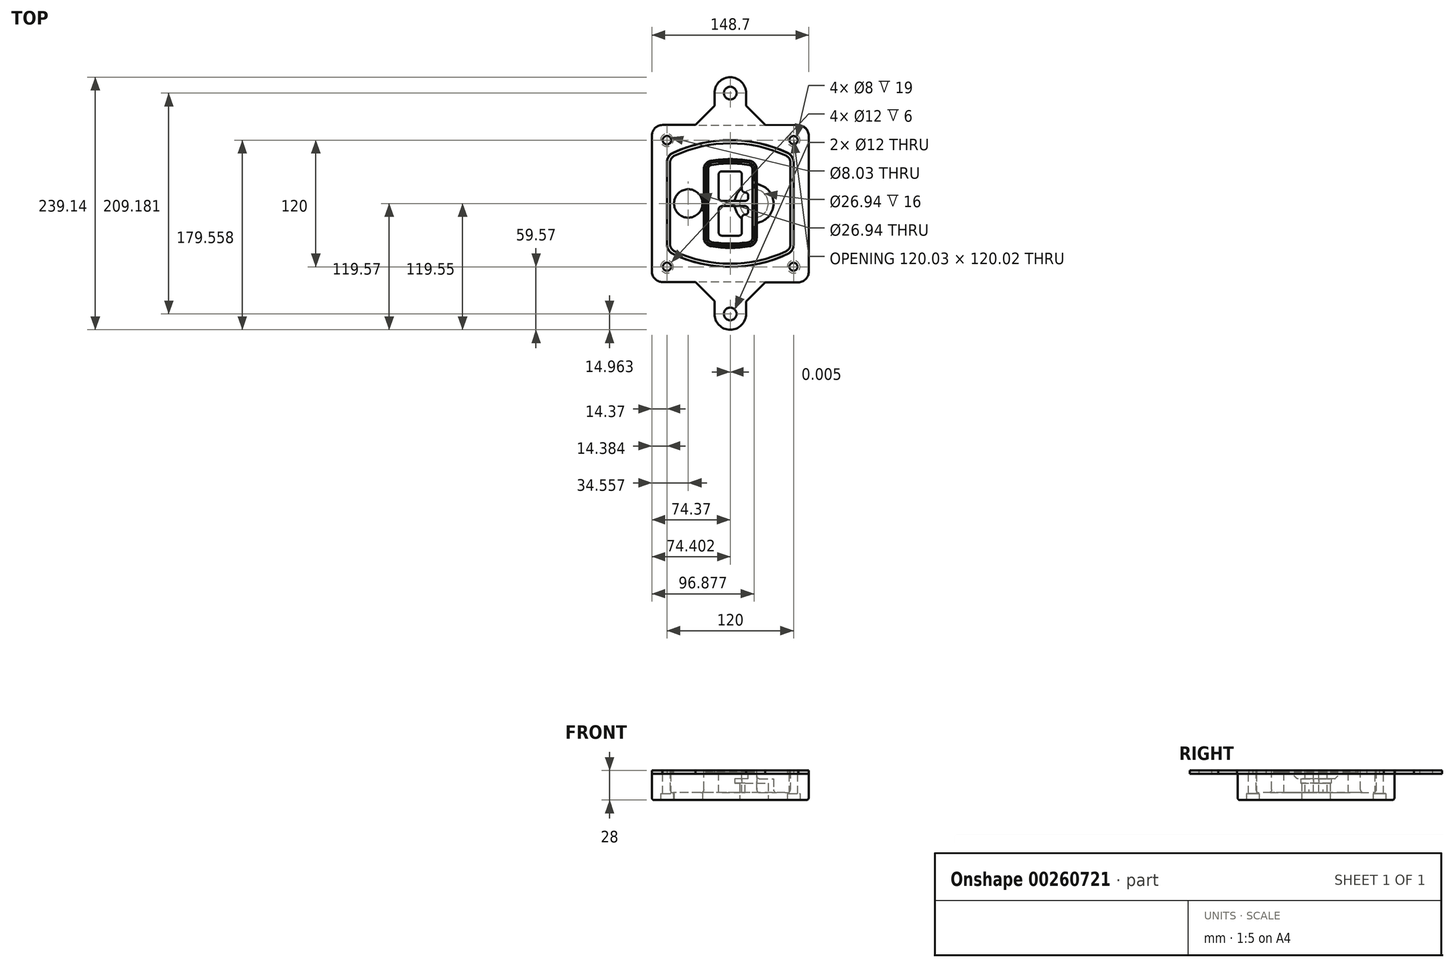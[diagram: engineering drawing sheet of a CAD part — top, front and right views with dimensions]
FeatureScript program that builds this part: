
annotation { "Feature Type Name" : "Feature", "Feature Type Description" : "" }
export const myFeature = defineFeature(function(context is Context, id is Id, definition is map)
    precondition{}
    {
        {
            var Q0;
            Q0=qCreatedBy(makeId("Top.planeOp"),FACE);
            var sketch = newSketch(context, id + "F0", { "sketchPlane" : qUnion([Q0])});
            skPoint(sketch, "E0.rect.middle", {"position": v(0, 0) * mm});
            skLineSegment(sketch, "E1.bottom", {"start": v(-64.25, -74.25) * mm, "end": v(64.25, -74.25) * mm});
            skLineSegment(sketch, "E1.top", {"start": v(-64.25, 74.25) * mm, "end": v(64.25, 74.25) * mm});
            skLineSegment(sketch, "E1.left", {"start": v(-74.25, -64.25) * mm, "end": v(-74.25, 64.25) * mm});
            skLineSegment(sketch, "E1.right", {"start": v(74.25, -64.25) * mm, "end": v(74.25, 64.25) * mm});
            skLineSegment(sketch, "E2", {"start": v(-74.25, 74.25) * mm, "end": v(74.25, -74.25) * mm, "construction": true});
            skLineSegment(sketch, "E3", {"start": v(74.25, 74.25) * mm, "end": v(-74.25, -74.25) * mm, "construction": true});
            skCircle(sketch, "E4", {"center": v(-60, 60) * mm, "radius": 4 * mm});
            skCircle(sketch, "E5", {"center": v(60, 60) * mm, "radius": 4 * mm});
            skCircle(sketch, "E6", {"center": v(60, -60) * mm, "radius": 4 * mm});
            skCircle(sketch, "E7", {"center": v(-60, -60) * mm, "radius": 4 * mm});
            skLineSegment(sketch, "E8", {"start": v(-60, 60) * mm, "end": v(60, 60) * mm, "construction": true});
            skLineSegment(sketch, "E9", {"start": v(60, 60) * mm, "end": v(60, -60) * mm, "construction": true});
            skLineSegment(sketch, "E10", {"start": v(60, -60) * mm, "end": v(-60, -60) * mm, "construction": true});
            skLineSegment(sketch, "E11", {"start": v(-60, -60) * mm, "end": v(-60, 60) * mm, "construction": true});
            skLineSegment(sketch, "E12", {"start": v(-60, 38.83) * mm, "end": v(-60, -38.83) * mm});
            skLineSegment(sketch, "E13", {"start": v(60, 38.83) * mm, "end": v(60, -38.83) * mm});
            skArc(sketch, "E14", {"start": v(54.26, 47.88) * mm, "mid": v(0, 60) * mm, "end": v(-54.26, 47.88) * mm});
            skArc(sketch, "E15", {"start": v(-54.26, -47.88) * mm, "mid": v(0, -60) * mm, "end": v(54.26, -47.88) * mm});
            skLineSegment(sketch, "E16", {"start": v(-60, 0) * mm, "end": v(60, 0) * mm, "construction": true});
            skPoint(sketch, "E17.visualSharp", {"position": v(-60, -45) * mm});
            skArc(sketch, "E17.filletArc", {"start": v(-60, -38.83) * mm, "mid": v(-58.44, -44.2) * mm, "end": v(-54.26, -47.88) * mm});
            skPoint(sketch, "E18.visualSharp", {"position": v(-60, 45) * mm});
            skArc(sketch, "E18.filletArc", {"start": v(-54.26, 47.88) * mm, "mid": v(-58.44, 44.2) * mm, "end": v(-60, 38.83) * mm});
            skPoint(sketch, "E19.visualSharp", {"position": v(60, 45) * mm});
            skArc(sketch, "E19.filletArc", {"start": v(60, 38.83) * mm, "mid": v(58.44, 44.2) * mm, "end": v(54.26, 47.88) * mm});
            skPoint(sketch, "E20.visualSharp", {"position": v(60, -45) * mm});
            skArc(sketch, "E20.filletArc", {"start": v(54.26, -47.88) * mm, "mid": v(58.44, -44.2) * mm, "end": v(60, -38.83) * mm});
            skPoint(sketch, "E21.visualSharp", {"position": v(-74.25, 74.25) * mm});
            skArc(sketch, "E21.filletArc", {"start": v(-64.25, 74.25) * mm, "mid": v(-71.32, 71.32) * mm, "end": v(-74.25, 64.25) * mm});
            skPoint(sketch, "E22.visualSharp", {"position": v(74.25, 74.25) * mm});
            skArc(sketch, "E22.filletArc", {"start": v(74.25, 64.25) * mm, "mid": v(71.32, 71.32) * mm, "end": v(64.25, 74.25) * mm});
            skPoint(sketch, "E23.visualSharp", {"position": v(74.25, -74.25) * mm});
            skArc(sketch, "E23.filletArc", {"start": v(64.25, -74.25) * mm, "mid": v(71.32, -71.32) * mm, "end": v(74.25, -64.25) * mm});
            skPoint(sketch, "E24.visualSharp", {"position": v(-74.25, -74.25) * mm});
            skArc(sketch, "E24.filletArc", {"start": v(-74.25, -64.25) * mm, "mid": v(-71.32, -71.32) * mm, "end": v(-64.25, -74.25) * mm});
            skArc(sketch, "E25.0", {"start": v(57, 38.83) * mm, "mid": v(55.9, 42.58) * mm, "end": v(52.98, 45.17) * mm});
            skLineSegment(sketch, "E25.1", {"start": v(57, 38.83) * mm, "end": v(57, -38.83) * mm});
            skArc(sketch, "E25.2", {"start": v(52.98, -45.17) * mm, "mid": v(55.9, -42.58) * mm, "end": v(57, -38.83) * mm});
            skArc(sketch, "E25.3", {"start": v(-52.98, -45.17) * mm, "mid": v(0, -57) * mm, "end": v(52.98, -45.17) * mm});
            skArc(sketch, "E25.4", {"start": v(-57, -38.83) * mm, "mid": v(-55.9, -42.58) * mm, "end": v(-52.98, -45.17) * mm});
            skArc(sketch, "E25.5", {"start": v(52.98, 45.17) * mm, "mid": v(0, 57) * mm, "end": v(-52.98, 45.17) * mm});
            skLineSegment(sketch, "E25.6", {"start": v(-57, 38.83) * mm, "end": v(-57, -38.83) * mm});
            skArc(sketch, "E25.7", {"start": v(-52.98, 45.17) * mm, "mid": v(-55.9, 42.58) * mm, "end": v(-57, 38.83) * mm});
            skArc(sketch, "E26.0", {"start": v(-55.96, 51.5) * mm, "mid": v(-61.82, 46.33) * mm, "end": v(-64, 38.83) * mm});
            skArc(sketch, "E26.1", {"start": v(55.96, 51.5) * mm, "mid": v(0, 64) * mm, "end": v(-55.96, 51.5) * mm});
            skArc(sketch, "E26.2", {"start": v(64, 38.83) * mm, "mid": v(61.82, 46.33) * mm, "end": v(55.96, 51.5) * mm});
            skLineSegment(sketch, "E26.3", {"start": v(64, 38.83) * mm, "end": v(64, -38.83) * mm});
            skArc(sketch, "E26.4", {"start": v(55.96, -51.5) * mm, "mid": v(61.82, -46.33) * mm, "end": v(64, -38.83) * mm});
            skLineSegment(sketch, "E26.5", {"start": v(-64, 38.83) * mm, "end": v(-64, -38.83) * mm});
            skArc(sketch, "E26.6", {"start": v(-55.96, -51.5) * mm, "mid": v(0, -64) * mm, "end": v(55.96, -51.5) * mm});
            skArc(sketch, "E26.7", {"start": v(-64, -38.83) * mm, "mid": v(-61.82, -46.33) * mm, "end": v(-55.96, -51.5) * mm});
            skSolve(sketch);
        }
        {
            var Q0;
            Q0=makeQuery(id+"F0.imprint","IMPRINT",FACE,{"disambiguationData":[TD([[makeQuery(id+"F0.imprint","IMPRINT",EDGE,{"derivedFrom":sQuery(id+"F0.wireOp",EDGE,"E1.bottom")}),1.0]])]});
            var Q1;
            Q1=makeQuery(id+"F0.imprint","IMPRINT",FACE,{"disambiguationData":[TD([[makeQuery(id+"F0.imprint","IMPRINT",EDGE,{"derivedFrom":sQuery(id+"F0.wireOp",EDGE,"E12")}),1.0]])]});
            var Q2;
            Q2=makeQuery(id+"F0.imprint","IMPRINT",FACE,{"disambiguationData":[TD([[makeQuery(id+"F0.imprint","IMPRINT",EDGE,{"derivedFrom":sQuery(id+"F0.wireOp",EDGE,"E25.0")}),1.0]])]});
            var Q3;
            Q3=makeQuery(id+"F0.imprint","IMPRINT",FACE,{"disambiguationData":[TD([[makeQuery(id+"F0.imprint","IMPRINT",EDGE,{"derivedFrom":sQuery(id+"F0.wireOp",EDGE,"E12")}),-1.0]])]});
            extrude(context, id + "F1", {"entities" : qUnion([Q0, Q1, Q2, Q3]), "oppositeDirection" : true, "depth" : 25 * mm});
        }
        {
            var Q0;
            Q0=makeQuery(id+"F0.imprint","IMPRINT",FACE,{"disambiguationData":[TD([[makeQuery(id+"F0.imprint","IMPRINT",EDGE,{"derivedFrom":sQuery(id+"F0.wireOp",EDGE,"E12")}),1.0]])]});
            extrude(context, id + "F2", {"entities" : qUnion([Q0]), "operationType" : NewBodyOperationType.ADD, "depth" : 3 * mm});
        }
        {
            var Q0;
            Q0=makeQuery(id+"F0.imprint","IMPRINT",FACE,{"disambiguationData":[TD([[makeQuery(id+"F0.imprint","IMPRINT",EDGE,{"derivedFrom":sQuery(id+"F0.wireOp",EDGE,"E25.0")}),1.0]])]});
            extrude(context, id + "F3", {"entities" : qUnion([Q0]), "operationType" : NewBodyOperationType.REMOVE, "oppositeDirection" : true, "depth" : 18 * mm});
        }
        {
            var Q0;
            Q0=makeQuery(id+"F2.opExtrude","CAP_FACE",FACE,{"disambiguationData":[OSD([sQuery(id+"F0.wireOp",EDGE,"E12"),sQuery(id+"F0.wireOp",EDGE,"E13"),sQuery(id+"F0.wireOp",EDGE,"E14"),sQuery(id+"F0.wireOp",EDGE,"E15"),sQuery(id+"F0.wireOp",EDGE,"E17.filletArc"),sQuery(id+"F0.wireOp",EDGE,"E18.filletArc"),sQuery(id+"F0.wireOp",EDGE,"E19.filletArc"),sQuery(id+"F0.wireOp",EDGE,"E20.filletArc"),sQuery(id+"F0.wireOp",EDGE,"E25.0"),sQuery(id+"F0.wireOp",EDGE,"E25.1"),sQuery(id+"F0.wireOp",EDGE,"E25.2"),sQuery(id+"F0.wireOp",EDGE,"E25.3"),sQuery(id+"F0.wireOp",EDGE,"E25.4"),sQuery(id+"F0.wireOp",EDGE,"E25.5"),sQuery(id+"F0.wireOp",EDGE,"E25.6"),sQuery(id+"F0.wireOp",EDGE,"E25.7")])],"isStart":false});
            var sketch = newSketch(context, id + "F4", { "sketchPlane" : qUnion([Q0])});
            skArc(sketch, "E27.0", {"start": v(-18.34, -40.45) * mm, "mid": v(0, -42) * mm, "end": v(18.34, -40.45) * mm});
            skArc(sketch, "E28.0", {"start": v(18.34, 40.45) * mm, "mid": v(0, 42) * mm, "end": v(-18.34, 40.45) * mm});
            skLineSegment(sketch, "E29", {"start": v(-25, 32.57) * mm, "end": v(-25, -32.57) * mm});
            skLineSegment(sketch, "E30", {"start": v(25, 32.57) * mm, "end": v(25, -32.57) * mm});
            skLineSegment(sketch, "E31", {"start": v(-25, 39.1) * mm, "end": v(25, 39.1) * mm, "construction": true});
            skLineSegment(sketch, "E32", {"start": v(-25, -39.1) * mm, "end": v(25, -39.1) * mm, "construction": true});
            skPoint(sketch, "E33.visualSharp", {"position": v(-25, 39.1) * mm});
            skArc(sketch, "E33.filletArc", {"start": v(-18.34, 40.45) * mm, "mid": v(-23.11, 37.73) * mm, "end": v(-25, 32.57) * mm});
            skPoint(sketch, "E34.visualSharp", {"position": v(25, 39.1) * mm});
            skArc(sketch, "E34.filletArc", {"start": v(25, 32.57) * mm, "mid": v(23.11, 37.73) * mm, "end": v(18.34, 40.45) * mm});
            skPoint(sketch, "E35.visualSharp", {"position": v(25, -39.1) * mm});
            skArc(sketch, "E35.filletArc", {"start": v(18.34, -40.45) * mm, "mid": v(23.11, -37.73) * mm, "end": v(25, -32.57) * mm});
            skPoint(sketch, "E36.visualSharp", {"position": v(-25, -39.1) * mm});
            skArc(sketch, "E36.filletArc", {"start": v(-25, -32.57) * mm, "mid": v(-23.11, -37.73) * mm, "end": v(-18.34, -40.45) * mm});
            skArc(sketch, "E37.0", {"start": v(52.98, 45.17) * mm, "mid": v(0, 57) * mm, "end": v(-52.98, 45.17) * mm});
            skArc(sketch, "E37.1", {"start": v(-52.98, 45.17) * mm, "mid": v(-55.9, 42.58) * mm, "end": v(-57, 38.83) * mm});
            skLineSegment(sketch, "E37.2", {"start": v(-57, 38.83) * mm, "end": v(-57, -38.83) * mm});
            skArc(sketch, "E37.3", {"start": v(-57, -38.83) * mm, "mid": v(-55.9, -42.58) * mm, "end": v(-52.98, -45.17) * mm});
            skArc(sketch, "E37.4", {"start": v(-52.98, -45.17) * mm, "mid": v(0, -57) * mm, "end": v(52.98, -45.17) * mm});
            skArc(sketch, "E37.5", {"start": v(52.98, -45.17) * mm, "mid": v(55.9, -42.58) * mm, "end": v(57, -38.83) * mm});
            skLineSegment(sketch, "E37.6", {"start": v(57, 38.83) * mm, "end": v(57, -38.83) * mm});
            skArc(sketch, "E37.7", {"start": v(57, 38.83) * mm, "mid": v(55.9, 42.58) * mm, "end": v(52.98, 45.17) * mm});
            skLineSegment(sketch, "E38.0", {"start": v(23, 32.57) * mm, "end": v(23, -32.57) * mm});
            skArc(sketch, "E38.1", {"start": v(18, -38.48) * mm, "mid": v(21.58, -36.44) * mm, "end": v(23, -32.57) * mm});
            skArc(sketch, "E38.2", {"start": v(-18, -38.48) * mm, "mid": v(0, -40) * mm, "end": v(18, -38.48) * mm});
            skArc(sketch, "E38.3", {"start": v(-23, -32.57) * mm, "mid": v(-21.58, -36.44) * mm, "end": v(-18, -38.48) * mm});
            skLineSegment(sketch, "E38.4", {"start": v(-23, 32.57) * mm, "end": v(-23, -32.57) * mm});
            skArc(sketch, "E38.5", {"start": v(23, 32.57) * mm, "mid": v(21.58, 36.44) * mm, "end": v(18, 38.48) * mm});
            skArc(sketch, "E38.6", {"start": v(-18, 38.48) * mm, "mid": v(-21.58, 36.44) * mm, "end": v(-23, 32.57) * mm});
            skArc(sketch, "E38.7", {"start": v(18, 38.48) * mm, "mid": v(0, 40) * mm, "end": v(-18, 38.48) * mm});
            skArc(sketch, "E39.0", {"start": v(21, 32.57) * mm, "mid": v(20.06, 35.15) * mm, "end": v(17.67, 36.5) * mm});
            skLineSegment(sketch, "E39.1", {"start": v(21, 32.57) * mm, "end": v(21, -32.57) * mm});
            skArc(sketch, "E39.2", {"start": v(17.67, -36.5) * mm, "mid": v(20.06, -35.15) * mm, "end": v(21, -32.57) * mm});
            skArc(sketch, "E39.3", {"start": v(-17.67, -36.5) * mm, "mid": v(0, -38) * mm, "end": v(17.67, -36.5) * mm});
            skArc(sketch, "E39.4", {"start": v(-21, -32.57) * mm, "mid": v(-20.06, -35.15) * mm, "end": v(-17.67, -36.5) * mm});
            skArc(sketch, "E39.5", {"start": v(17.67, 36.5) * mm, "mid": v(0, 38) * mm, "end": v(-17.67, 36.5) * mm});
            skLineSegment(sketch, "E39.6", {"start": v(-21, 32.57) * mm, "end": v(-21, -32.57) * mm});
            skArc(sketch, "E39.7", {"start": v(-17.67, 36.5) * mm, "mid": v(-20.06, 35.15) * mm, "end": v(-21, 32.57) * mm});
            skLineSegment(sketch, "E40", {"start": v(-25, 0) * mm, "end": v(25, 0) * mm, "construction": true});
            skLineSegment(sketch, "E41", {"start": v(-11, 5.5) * mm, "end": v(-11, 27.5) * mm});
            skLineSegment(sketch, "E42", {"start": v(-8, 30.5) * mm, "end": v(8, 30.5) * mm});
            skLineSegment(sketch, "E43", {"start": v(11, 27.5) * mm, "end": v(11, 13.5) * mm});
            skLineSegment(sketch, "E44", {"start": v(14, 10.5) * mm, "end": v(14, 10.5) * mm});
            skLineSegment(sketch, "E45", {"start": v(17, 7.5) * mm, "end": v(17, 5.5) * mm});
            skLineSegment(sketch, "E46", {"start": v(14, 2.5) * mm, "end": v(-8, 2.5) * mm});
            skPoint(sketch, "E47.visualSharp", {"position": v(-11, 30.5) * mm});
            skArc(sketch, "E47.filletArc", {"start": v(-8, 30.5) * mm, "mid": v(-10.12, 29.62) * mm, "end": v(-11, 27.5) * mm});
            skPoint(sketch, "E48.visualSharp", {"position": v(11, 30.5) * mm});
            skArc(sketch, "E48.filletArc", {"start": v(11, 27.5) * mm, "mid": v(10.12, 29.62) * mm, "end": v(8, 30.5) * mm});
            skPoint(sketch, "E49.visualSharp", {"position": v(11, 10.5) * mm});
            skArc(sketch, "E49.filletArc", {"start": v(11, 13.5) * mm, "mid": v(11.88, 11.38) * mm, "end": v(14, 10.5) * mm});
            skPoint(sketch, "E50.visualSharp", {"position": v(17, 10.5) * mm});
            skArc(sketch, "E50.filletArc", {"start": v(17, 7.5) * mm, "mid": v(16.12, 9.62) * mm, "end": v(14, 10.5) * mm});
            skPoint(sketch, "E51.visualSharp", {"position": v(17, 2.5) * mm});
            skArc(sketch, "E51.filletArc", {"start": v(14, 2.5) * mm, "mid": v(16.12, 3.38) * mm, "end": v(17, 5.5) * mm});
            skPoint(sketch, "E52.visualSharp", {"position": v(-11, 2.5) * mm});
            skArc(sketch, "E52.filletArc", {"start": v(-11, 5.5) * mm, "mid": v(-10.12, 3.38) * mm, "end": v(-8, 2.5) * mm});
            skLineSegment(sketch, "E53.0.MirrorCS", {"start": v(14, -2.5) * mm, "end": v(-8, -2.5) * mm});
            skArc(sketch, "E54.0.MirrorCS", {"start": v(-11, -5.5) * mm, "mid": v(-10.12, -3.38) * mm, "end": v(-8, -2.5) * mm});
            skLineSegment(sketch, "E55.0.MirrorCS", {"start": v(-11, -5.5) * mm, "end": v(-11, -27.5) * mm});
            skArc(sketch, "E56.0.MirrorCS", {"start": v(-8, -30.5) * mm, "mid": v(-10.12, -29.62) * mm, "end": v(-11, -27.5) * mm});
            skLineSegment(sketch, "E57.0.MirrorCS", {"start": v(-8, -30.5) * mm, "end": v(8, -30.5) * mm});
            skArc(sketch, "E58.0.MirrorCS", {"start": v(11, -27.5) * mm, "mid": v(10.12, -29.62) * mm, "end": v(8, -30.5) * mm});
            skLineSegment(sketch, "E59.0.MirrorCS", {"start": v(11, -27.5) * mm, "end": v(11, -13.5) * mm});
            skArc(sketch, "E60.0.MirrorCS", {"start": v(11, -13.5) * mm, "mid": v(11.88, -11.38) * mm, "end": v(14, -10.5) * mm});
            skArc(sketch, "E61.0.MirrorCS", {"start": v(17, -7.5) * mm, "mid": v(16.12, -9.62) * mm, "end": v(14, -10.5) * mm});
            skLineSegment(sketch, "E62.0.MirrorCS", {"start": v(17, -7.5) * mm, "end": v(17, -5.5) * mm});
            skArc(sketch, "E63.0.MirrorCS", {"start": v(14, -2.5) * mm, "mid": v(16.12, -3.38) * mm, "end": v(17, -5.5) * mm});
            skSolve(sketch);
        }
        {
            var Q0;
            Q0=makeQuery(id+"F4.imprint","IMPRINT",FACE,{"disambiguationData":[TD([[makeQuery(id+"F4.imprint","IMPRINT",EDGE,{"derivedFrom":sQuery(id+"F4.wireOp",EDGE,"E27.0")}),1.0]])]});
            var Q1;
            Q1=makeQuery(id+"F4.imprint","IMPRINT",FACE,{"disambiguationData":[TD([[makeQuery(id+"F4.imprint","IMPRINT",EDGE,{"derivedFrom":sQuery(id+"F4.wireOp",EDGE,"E38.0")}),-1.0]])]});
            var Q2;
            Q2=makeQuery(id+"F4.imprint","IMPRINT",FACE,{"disambiguationData":[TD([[makeQuery(id+"F4.imprint","IMPRINT",EDGE,{"derivedFrom":sQuery(id+"F4.wireOp",EDGE,"E39.0")}),1.0]])]});
            extrude(context, id + "F5", {"entities" : qUnion([Q0, Q1, Q2]), "operationType" : NewBodyOperationType.ADD, "endBound" : BoundingType.UP_TO_NEXT, "oppositeDirection" : true, "depth" : 25 * mm});
        }
        {
            var Q0;
            Q0=makeQuery(id+"F4.imprint","IMPRINT",FACE,{"disambiguationData":[TD([[makeQuery(id+"F4.imprint","IMPRINT",EDGE,{"derivedFrom":sQuery(id+"F4.wireOp",EDGE,"E38.0")}),-1.0]])]});
            extrude(context, id + "F6", {"entities" : qUnion([Q0]), "operationType" : NewBodyOperationType.REMOVE, "oppositeDirection" : true, "depth" : 2 * mm});
        }
        {
            var Q0;
            Q0=makeQuery(id+"F1.opExtrude","CAP_FACE",FACE,{"disambiguationData":[OSD([sQuery(id+"F0.wireOp",EDGE,"E1.bottom"),sQuery(id+"F0.wireOp",EDGE,"E1.top"),sQuery(id+"F0.wireOp",EDGE,"E1.left"),sQuery(id+"F0.wireOp",EDGE,"E1.right"),sQuery(id+"F0.wireOp",EDGE,"E4"),sQuery(id+"F0.wireOp",EDGE,"E5"),sQuery(id+"F0.wireOp",EDGE,"E6"),sQuery(id+"F0.wireOp",EDGE,"E7"),sQuery(id+"F0.wireOp",EDGE,"E21.filletArc"),sQuery(id+"F0.wireOp",EDGE,"E22.filletArc"),sQuery(id+"F0.wireOp",EDGE,"E23.filletArc"),sQuery(id+"F0.wireOp",EDGE,"E24.filletArc")])],"isStart":false});
            var sketch = newSketch(context, id + "F7", { "sketchPlane" : qUnion([Q0])});
            skCircle(sketch, "E64", {"center": v(22.5, 0) * mm, "radius": 13.47 * mm});
            skCircle(sketch, "E65", {"center": v(-39.81, 0) * mm, "radius": 13.47 * mm});
            skLineSegment(sketch, "E66", {"start": v(74.25, 0) * mm, "end": v(-74.25, 0) * mm});
            skCircle(sketch, "E67", {"center": v(22.5, 0) * mm, "radius": 18.47 * mm});
            skCircle(sketch, "E68", {"center": v(60, -60) * mm, "radius": 6 * mm});
            skCircle(sketch, "E69", {"center": v(-60, -60) * mm, "radius": 6 * mm});
            skCircle(sketch, "E70", {"center": v(-60, 60) * mm, "radius": 6 * mm});
            skCircle(sketch, "E71", {"center": v(60, 60) * mm, "radius": 6 * mm});
            skSolve(sketch);
        }
        {
            var Q0;
            {var subQ1=sQuery(id+"F7.wireOp",EDGE,"E66");var subQ4=sQuery(id+"F7.wireOp",EDGE,"E64");var subQ6=makeQuery(id+"F7.imprint","INTERSECT",VERTEX,{"disambiguationData":[OD(0.0)],"derivedFrom":[subQ4,subQ1]});Q0=makeQuery(id+"F7.imprint","IMPRINT",FACE,{"disambiguationData":[TD([[makeQuery(id+"F7.imprint","IMPRINT",EDGE,{"disambiguationData":[TD([[subQ6,-1.0]])],"derivedFrom":subQ4}),-1.0]])]});}
            var Q1;
            {var subQ0=sQuery(id+"F7.wireOp",EDGE,"E66");var subQ1=sQuery(id+"F7.wireOp",EDGE,"E64");var subQ3=makeQuery(id+"F7.imprint","INTERSECT",VERTEX,{"disambiguationData":[OD(0.0)],"derivedFrom":[subQ1,subQ0]});Q1=makeQuery(id+"F7.imprint","IMPRINT",FACE,{"disambiguationData":[TD([[makeQuery(id+"F7.imprint","IMPRINT",EDGE,{"disambiguationData":[TD([[subQ3,-1.0]])],"derivedFrom":subQ1}),1.0]])]});}
            var Q2;
            {var subQ0=sQuery(id+"F7.wireOp",EDGE,"E66");var subQ1=sQuery(id+"F7.wireOp",EDGE,"E64");var subQ3=makeQuery(id+"F7.imprint","INTERSECT",VERTEX,{"disambiguationData":[OD(0.0)],"derivedFrom":[subQ1,subQ0]});Q2=makeQuery(id+"F7.imprint","IMPRINT",FACE,{"disambiguationData":[TD([[makeQuery(id+"F7.imprint","IMPRINT",EDGE,{"disambiguationData":[TD([[subQ3,1.0]])],"derivedFrom":subQ1}),1.0]])]});}
            var Q3;
            {var subQ1=sQuery(id+"F7.wireOp",EDGE,"E66");var subQ4=sQuery(id+"F7.wireOp",EDGE,"E64");var subQ6=makeQuery(id+"F7.imprint","INTERSECT",VERTEX,{"disambiguationData":[OD(0.0)],"derivedFrom":[subQ4,subQ1]});Q3=makeQuery(id+"F7.imprint","IMPRINT",FACE,{"disambiguationData":[TD([[makeQuery(id+"F7.imprint","IMPRINT",EDGE,{"disambiguationData":[TD([[subQ6,1.0]])],"derivedFrom":subQ4}),-1.0]])]});}
            extrude(context, id + "F8", {"entities" : qUnion([Q0, Q1, Q2, Q3]), "operationType" : NewBodyOperationType.ADD, "oppositeDirection" : true, "depth" : 20 * mm});
        }
        {
            var Q0;
            {var subQ0=sQuery(id+"F7.wireOp",EDGE,"E66");var subQ1=sQuery(id+"F7.wireOp",EDGE,"E64");var subQ3=makeQuery(id+"F7.imprint","INTERSECT",VERTEX,{"disambiguationData":[OD(0.0)],"derivedFrom":[subQ1,subQ0]});Q0=makeQuery(id+"F7.imprint","IMPRINT",FACE,{"disambiguationData":[TD([[makeQuery(id+"F7.imprint","IMPRINT",EDGE,{"disambiguationData":[TD([[subQ3,-1.0]])],"derivedFrom":subQ1}),1.0]])]});}
            var Q1;
            {var subQ0=sQuery(id+"F7.wireOp",EDGE,"E66");var subQ1=sQuery(id+"F7.wireOp",EDGE,"E64");var subQ3=makeQuery(id+"F7.imprint","INTERSECT",VERTEX,{"disambiguationData":[OD(0.0)],"derivedFrom":[subQ1,subQ0]});Q1=makeQuery(id+"F7.imprint","IMPRINT",FACE,{"disambiguationData":[TD([[makeQuery(id+"F7.imprint","IMPRINT",EDGE,{"disambiguationData":[TD([[subQ3,1.0]])],"derivedFrom":subQ1}),1.0]])]});}
            extrude(context, id + "F9", {"entities" : qUnion([Q0, Q1]), "operationType" : NewBodyOperationType.REMOVE, "oppositeDirection" : true, "depth" : 16 * mm});
        }
        {
            var Q0;
            {var subQ0=sQuery(id+"F7.wireOp",EDGE,"E66");var subQ1=sQuery(id+"F7.wireOp",EDGE,"E65");var subQ3=makeQuery(id+"F7.imprint","INTERSECT",VERTEX,{"disambiguationData":[OD(0.0)],"derivedFrom":[subQ1,subQ0]});Q0=makeQuery(id+"F7.imprint","IMPRINT",FACE,{"disambiguationData":[TD([[makeQuery(id+"F7.imprint","IMPRINT",EDGE,{"disambiguationData":[TD([[subQ3,-1.0]])],"derivedFrom":subQ1}),1.0]])]});}
            var Q1;
            {var subQ0=sQuery(id+"F7.wireOp",EDGE,"E66");var subQ1=sQuery(id+"F7.wireOp",EDGE,"E65");var subQ3=makeQuery(id+"F7.imprint","INTERSECT",VERTEX,{"disambiguationData":[OD(0.0)],"derivedFrom":[subQ1,subQ0]});Q1=makeQuery(id+"F7.imprint","IMPRINT",FACE,{"disambiguationData":[TD([[makeQuery(id+"F7.imprint","IMPRINT",EDGE,{"disambiguationData":[TD([[subQ3,1.0]])],"derivedFrom":subQ1}),1.0]])]});}
            extrude(context, id + "F10", {"entities" : qUnion([Q0, Q1]), "operationType" : NewBodyOperationType.REMOVE, "oppositeDirection" : true, "depth" : 25 * mm});
        }
        {
            var Q0;
            Q0=makeQuery(id+"F7.imprint","IMPRINT",FACE,{"disambiguationData":[TD([[makeQuery(id+"F7.imprint","IMPRINT",EDGE,{"derivedFrom":sQuery(id+"F7.wireOp",EDGE,"E68")}),1.0]])]});
            var Q1;
            Q1=makeQuery(id+"F7.imprint","IMPRINT",FACE,{"disambiguationData":[TD([[makeQuery(id+"F7.imprint","IMPRINT",EDGE,{"derivedFrom":makeQuery(id+"F1.opExtrude","CAP_EDGE",EDGE,{"disambiguationData":[OSD([sQuery(id+"F0.wireOp",EDGE,"E5")])],"isStart":false})}),-1.0]])]});
            var Q2;
            Q2=makeQuery(id+"F7.imprint","IMPRINT",FACE,{"disambiguationData":[TD([[makeQuery(id+"F7.imprint","IMPRINT",EDGE,{"derivedFrom":sQuery(id+"F7.wireOp",EDGE,"E69")}),1.0]])]});
            var Q3;
            Q3=makeQuery(id+"F7.imprint","IMPRINT",FACE,{"disambiguationData":[TD([[makeQuery(id+"F7.imprint","IMPRINT",EDGE,{"derivedFrom":makeQuery(id+"F1.opExtrude","CAP_EDGE",EDGE,{"disambiguationData":[OSD([sQuery(id+"F0.wireOp",EDGE,"E4")])],"isStart":false})}),-1.0]])]});
            var Q4;
            Q4=makeQuery(id+"F7.imprint","IMPRINT",FACE,{"disambiguationData":[TD([[makeQuery(id+"F7.imprint","IMPRINT",EDGE,{"derivedFrom":sQuery(id+"F7.wireOp",EDGE,"E70")}),1.0]])]});
            var Q5;
            Q5=makeQuery(id+"F7.imprint","IMPRINT",FACE,{"disambiguationData":[TD([[makeQuery(id+"F7.imprint","IMPRINT",EDGE,{"derivedFrom":makeQuery(id+"F1.opExtrude","CAP_EDGE",EDGE,{"disambiguationData":[OSD([sQuery(id+"F0.wireOp",EDGE,"E7")])],"isStart":false})}),-1.0]])]});
            var Q6;
            Q6=makeQuery(id+"F7.imprint","IMPRINT",FACE,{"disambiguationData":[TD([[makeQuery(id+"F7.imprint","IMPRINT",EDGE,{"derivedFrom":sQuery(id+"F7.wireOp",EDGE,"E71")}),1.0]])]});
            var Q7;
            Q7=makeQuery(id+"F7.imprint","IMPRINT",FACE,{"disambiguationData":[TD([[makeQuery(id+"F7.imprint","IMPRINT",EDGE,{"derivedFrom":makeQuery(id+"F1.opExtrude","CAP_EDGE",EDGE,{"disambiguationData":[OSD([sQuery(id+"F0.wireOp",EDGE,"E6")])],"isStart":false})}),-1.0]])]});
            extrude(context, id + "F11", {"entities" : qUnion([Q0, Q1, Q2, Q3, Q4, Q5, Q6, Q7]), "operationType" : NewBodyOperationType.REMOVE, "oppositeDirection" : true, "depth" : 6 * mm});
        }
        {
            var Q0;
            Q0=makeQuery(id+"F9.boolean.opBoolean","COPY",FACE,{"derivedFrom":makeQuery(id+"F9.opExtrude","CAP_FACE",FACE,{"disambiguationData":[OSD([sQuery(id+"F7.wireOp",EDGE,"E64")])],"isStart":false})});
            var sketch = newSketch(context, id + "F12", { "sketchPlane" : qUnion([Q0])});
            skArc(sketch, "E72.0", {"start": v(11, 14.45) * mm, "mid": v(6.45, 9.13) * mm, "end": v(4.2, 2.5) * mm});
            skArc(sketch, "E72.1", {"start": v(4.2, -2.5) * mm, "mid": v(6.45, -9.13) * mm, "end": v(11, -14.45) * mm});
            skLineSegment(sketch, "E73", {"start": v(4.2, -2.5) * mm, "end": v(14, -2.5) * mm});
            skLineSegment(sketch, "E74.0", {"start": v(14, 2.5) * mm, "end": v(4.2, 2.5) * mm});
            skArc(sketch, "E74.1", {"start": v(14, 2.5) * mm, "mid": v(16.12, 3.38) * mm, "end": v(17, 5.5) * mm});
            skLineSegment(sketch, "E74.2", {"start": v(17, 7.5) * mm, "end": v(17, 5.5) * mm});
            skArc(sketch, "E74.3", {"start": v(17, 7.5) * mm, "mid": v(16.12, 9.62) * mm, "end": v(14, 10.5) * mm});
            skArc(sketch, "E74.4", {"start": v(11, 13.5) * mm, "mid": v(11.88, 11.38) * mm, "end": v(14, 10.5) * mm});
            skLineSegment(sketch, "E74.5", {"start": v(11, 14.45) * mm, "end": v(11, 13.5) * mm});
            skLineSegment(sketch, "E74.7", {"start": v(14, -2.5) * mm, "end": v(4.2, -2.5) * mm});
            skArc(sketch, "E74.8", {"start": v(14, -2.5) * mm, "mid": v(16.12, -3.38) * mm, "end": v(17, -5.5) * mm});
            skLineSegment(sketch, "E74.9", {"start": v(17, -7.5) * mm, "end": v(17, -5.5) * mm});
            skArc(sketch, "E74.10", {"start": v(17, -7.5) * mm, "mid": v(16.12, -9.62) * mm, "end": v(14, -10.5) * mm});
            skArc(sketch, "E74.11", {"start": v(11, -13.5) * mm, "mid": v(11.88, -11.38) * mm, "end": v(14, -10.5) * mm});
            skLineSegment(sketch, "E74.12", {"start": v(11, -14.45) * mm, "end": v(11, -13.5) * mm});
            skPoint(sketch, "E75.orphan", {"position": v(11, -27.5) * mm});
            skPoint(sketch, "E76.orphan", {"position": v(-8, -2.5) * mm});
            skPoint(sketch, "E77.orphan", {"position": v(-8, 2.5) * mm});
            skPoint(sketch, "E78.orphan", {"position": v(11, 27.5) * mm});
            skSolve(sketch);
        }
        {
            var Q0;
            {var subQ7=sQuery(id+"F12.wireOp",EDGE,"E72.0");var subQ14=sQuery(id+"F12.wireOp",EDGE,"E72.1");var subQ16=sQuery(id+"F12.wireOp",EDGE,"E74.1");var subQ18=sQuery(id+"F12.wireOp",EDGE,"E74.8");Q0=qUnion([makeQuery(id+"F12.imprint","IMPRINT",FACE,{"disambiguationData":[TD([[makeQuery(id+"F12.imprint","IMPRINT",EDGE,{"derivedFrom":subQ7}),1.0]])]}),makeQuery(id+"F12.imprint","IMPRINT",FACE,{"disambiguationData":[TD([[makeQuery(id+"F12.imprint","IMPRINT",EDGE,{"derivedFrom":subQ14}),1.0]])]}),makeQuery(id+"F12.imprint","IMPRINT",FACE,{"disambiguationData":[TD([[makeQuery(id+"F12.imprint","IMPRINT",EDGE,{"derivedFrom":subQ16}),1.0]])]}),makeQuery(id+"F12.imprint","IMPRINT",FACE,{"disambiguationData":[TD([[makeQuery(id+"F12.imprint","IMPRINT",EDGE,{"derivedFrom":subQ18}),-1.0]])]})]);}
            var Q1;
            Q1=makeQuery(id+"F5.boolean.opBoolean","SPLIT",FACE,{"disambiguationData":[TD([makeQuery(id+"F5.opExtrude","SWEPT_FACE",FACE,{"disambiguationData":[OSD([sQuery(id+"F4.wireOp",EDGE,"E41")])]})])],"derivedFrom":makeQuery(id+"F3.boolean.opBoolean","COPY",FACE,{"derivedFrom":makeQuery(id+"F3.opExtrude","CAP_FACE",FACE,{"disambiguationData":[OSD([sQuery(id+"F0.wireOp",EDGE,"E25.0"),sQuery(id+"F0.wireOp",EDGE,"E25.1"),sQuery(id+"F0.wireOp",EDGE,"E25.2"),sQuery(id+"F0.wireOp",EDGE,"E25.3"),sQuery(id+"F0.wireOp",EDGE,"E25.4"),sQuery(id+"F0.wireOp",EDGE,"E25.5"),sQuery(id+"F0.wireOp",EDGE,"E25.6"),sQuery(id+"F0.wireOp",EDGE,"E25.7")])],"isStart":false})})});
            extrude(context, id + "F13", {"entities" : qUnion([Q0]), "operationType" : NewBodyOperationType.REMOVE, "endBound" : BoundingType.UP_TO_SURFACE, "endBoundEntityFace" : qUnion([Q1]), "depth" : 25 * mm});
        }
        {
            var Q0;
            Q0=makeQuery(id+"F3.boolean.opBoolean","COPY",EDGE,{"derivedFrom":makeQuery(id+"F3.opExtrude","CAP_EDGE",EDGE,{"disambiguationData":[OSD([sQuery(id+"F0.wireOp",EDGE,"E25.6")])],"isStart":false})});
            var Q1;
            Q1=makeQuery(id+"F8.boolean.opBoolean","INTERSECT",EDGE,{"derivedFrom":[makeQuery(id+"F5.opExtrude","SWEPT_FACE",FACE,{"disambiguationData":[OSD([sQuery(id+"F4.wireOp",EDGE,"E30")])]}),makeQuery(id+"F8.opExtrude","CAP_FACE",FACE,{"disambiguationData":[OSD([sQuery(id+"F7.wireOp",EDGE,"E67")])],"isStart":false})]});
            var Q2;
            Q2=makeQuery(id+"F8.boolean.opBoolean","INTERSECT",EDGE,{"disambiguationData":[OD(1.0)],"derivedFrom":[makeQuery(id+"F5.opExtrude","SWEPT_FACE",FACE,{"disambiguationData":[OSD([sQuery(id+"F4.wireOp",EDGE,"E30")])]}),makeQuery(id+"F8.opExtrude","SWEPT_FACE",FACE,{"disambiguationData":[OSD([sQuery(id+"F7.wireOp",EDGE,"E67")])]})]});
            var Q3;
            {var subQ0=sQuery(id+"F4.wireOp",EDGE,"E30");Q3=makeQuery(id+"F8.boolean.opBoolean","SPLIT",EDGE,{"disambiguationData":[TD([makeQuery(id+"F5.opExtrude","SWEPT_FACE",FACE,{"disambiguationData":[OSD([sQuery(id+"F4.wireOp",EDGE,"E35.filletArc")])]})])],"derivedFrom":makeQuery(id+"F5.opExtrude","CAP_EDGE",EDGE,{"disambiguationData":[OSD([subQ0])],"isStart":false})});}
            var Q4;
            {var subQ0=sQuery(id+"F0.wireOp",EDGE,"E25.7");var subQ1=sQuery(id+"F0.wireOp",EDGE,"E25.1");var subQ2=sQuery(id+"F0.wireOp",EDGE,"E25.6");var subQ3=sQuery(id+"F0.wireOp",EDGE,"E25.5");var subQ4=sQuery(id+"F0.wireOp",EDGE,"E25.4");var subQ5=sQuery(id+"F0.wireOp",EDGE,"E25.0");var subQ6=sQuery(id+"F0.wireOp",EDGE,"E25.2");var subQ7=sQuery(id+"F0.wireOp",EDGE,"E25.3");Q4=makeQuery(id+"F8.boolean.opBoolean","INTERSECT",EDGE,{"derivedFrom":[makeQuery(id+"F5.boolean.opBoolean","SPLIT",FACE,{"disambiguationData":[TD([makeQuery(id+"F2.opExtrude","SWEPT_FACE",FACE,{"disambiguationData":[OSD([subQ5])]})])],"derivedFrom":makeQuery(id+"F3.boolean.opBoolean","COPY",FACE,{"derivedFrom":makeQuery(id+"F3.opExtrude","CAP_FACE",FACE,{"disambiguationData":[OSD([subQ5,subQ1,subQ6,subQ7,subQ4,subQ3,subQ2,subQ0])],"isStart":false})})}),makeQuery(id+"F8.opExtrude","SWEPT_FACE",FACE,{"disambiguationData":[OSD([sQuery(id+"F7.wireOp",EDGE,"E67")])]})]});}
            var Q5;
            Q5=makeQuery(id+"F8.boolean.opBoolean","INTERSECT",EDGE,{"disambiguationData":[OD(0.0)],"derivedFrom":[makeQuery(id+"F5.opExtrude","SWEPT_FACE",FACE,{"disambiguationData":[OSD([sQuery(id+"F4.wireOp",EDGE,"E30")])]}),makeQuery(id+"F8.opExtrude","SWEPT_FACE",FACE,{"disambiguationData":[OSD([sQuery(id+"F7.wireOp",EDGE,"E67")])]})]});
            fillet(context, id + "F14", {"entities" : qUnion([Q0, Q1, Q2, Q3, Q4, Q5]), "radius" : 3 * mm, "tangentPropagation" : true, "allowEdgeOverflow" : false});
        }
        {
            var Q0;
            Q0=makeQuery(id+"F1.opExtrude","CAP_EDGE",EDGE,{"disambiguationData":[OSD([sQuery(id+"F0.wireOp",EDGE,"E1.bottom")])],"isStart":false});
            fillet(context, id + "F15", {"entities" : qUnion([Q0]), "radius" : 2 * mm, "tangentPropagation" : true, "allowEdgeOverflow" : false});
        }
        {
            var Q0;
            {var subQ0=sQuery(id+"F0.wireOp",EDGE,"E22.filletArc");var subQ1=sQuery(id+"F0.wireOp",EDGE,"E7");var subQ2=sQuery(id+"F0.wireOp",EDGE,"E6");var subQ3=sQuery(id+"F0.wireOp",EDGE,"E5");var subQ4=sQuery(id+"F0.wireOp",EDGE,"E4");var subQ5=sQuery(id+"F0.wireOp",EDGE,"E1.bottom");var subQ6=sQuery(id+"F0.wireOp",EDGE,"E21.filletArc");var subQ7=sQuery(id+"F0.wireOp",EDGE,"E1.top");var subQ8=sQuery(id+"F0.wireOp",EDGE,"E1.left");var subQ9=sQuery(id+"F0.wireOp",EDGE,"E1.right");var subQ10=sQuery(id+"F0.wireOp",EDGE,"E23.filletArc");var subQ11=sQuery(id+"F0.wireOp",EDGE,"E24.filletArc");Q0=makeQuery(id+"F2.boolean.opBoolean","SPLIT",FACE,{"disambiguationData":[TD([makeQuery(id+"F1.opExtrude","SWEPT_FACE",FACE,{"disambiguationData":[OSD([subQ5])]})])],"derivedFrom":makeQuery(id+"F1.opExtrude","CAP_FACE",FACE,{"disambiguationData":[OSD([subQ5,subQ7,subQ8,subQ9,subQ4,subQ3,subQ2,subQ1,subQ6,subQ0,subQ10,subQ11])],"isStart":true})});}
            var sketch = newSketch(context, id + "F16", { "sketchPlane" : qUnion([Q0])});
            skSolve(sketch);
        }
        {
            var Q0;
            Q0=makeQuery(id+"F16.imprint","IMPRINT",FACE,{"disambiguationData":[TD([[makeQuery(id+"F16.imprint","IMPRINT",EDGE,{"derivedFrom":makeQuery(id+"F1.opExtrude","CAP_EDGE",EDGE,{"disambiguationData":[OSD([sQuery(id+"F0.wireOp",EDGE,"E1.bottom")])],"isStart":true})}),1.0]])]});
            var sketch = newSketch(context, id + "F17", { "sketchPlane" : qUnion([Q0])});
            skArc(sketch, "E79", {"start": v(-64.17, 74.37) * mm, "mid": v(-71.23, 71.47) * mm, "end": v(-74.24, 64.44) * mm});
            skArc(sketch, "E80", {"start": v(74.33, 64.29) * mm, "mid": v(71.38, 71.12) * mm, "end": v(64.62, 74.23) * mm});
            skLineSegment(sketch, "E81", {"start": v(74.33, 64.29) * mm, "end": v(74.33, -64.52) * mm});
            skArc(sketch, "E82", {"start": v(64.6, -74.75) * mm, "mid": v(71.5, -71.58) * mm, "end": v(74.33, -64.52) * mm});
            skLineSegment(sketch, "E83", {"start": v(-74.37, -64.15) * mm, "end": v(-74.24, 64.44) * mm});
            skLineSegment(sketch, "E84", {"start": v(-32.98, -74.53) * mm, "end": v(-15.02, -92.57) * mm});
            skLineSegment(sketch, "E85", {"start": v(33.01, -74.68) * mm, "end": v(14.97, -92.64) * mm});
            skLineSegment(sketch, "E86", {"start": v(0, -74.6) * mm, "end": v(-0.07, -104.6) * mm});
            skCircle(sketch, "E87", {"center": v(-0.07, -104.6) * mm, "radius": 15 * mm, "construction": true});
            skLineSegment(sketch, "E88", {"start": v(-15.07, -104.6) * mm, "end": v(-15.07, -92.57) * mm});
            skLineSegment(sketch, "E89", {"start": v(14.93, -104.6) * mm, "end": v(14.93, -92.64) * mm});
            skCircle(sketch, "E90", {"center": v(-60, -59.92) * mm, "radius": 3.88 * mm});
            skCircle(sketch, "E91", {"center": v(59.86, -59.96) * mm, "radius": 3.84 * mm});
            skCircle(sketch, "E92", {"center": v(59.97, 60) * mm, "radius": 3.92 * mm});
            skCircle(sketch, "E93", {"center": v(-59.99, 59.99) * mm, "radius": 4.01 * mm});
            skLineSegment(sketch, "E94", {"start": v(0, 0) * mm, "end": v(74.33, -0.08) * mm});
            skLineSegment(sketch, "E95.MirrorCS", {"start": v(0.15, 74.6) * mm, "end": v(0.15, 104.6) * mm});
            skLineSegment(sketch, "E96.MirrorCS", {"start": v(-32.82, 74.6) * mm, "end": v(-14.82, 92.6) * mm});
            skLineSegment(sketch, "E97.MirrorCS", {"start": v(33.17, 74.61) * mm, "end": v(15.16, 92.6) * mm});
            skLineSegment(sketch, "E98.MirrorCS", {"start": v(15.15, 104.58) * mm, "end": v(15.13, 92.6) * mm});
            skCircle(sketch, "E99.MirrorC", {"center": v(0.15, 104.6) * mm, "radius": 15 * mm, "construction": true});
            skLineSegment(sketch, "E100.MirrorCS", {"start": v(-14.85, 104.64) * mm, "end": v(-14.87, 92.6) * mm});
            skArc(sketch, "E101", {"start": v(-53.93, 48.07) * mm, "mid": v(-58.36, 44.7) * mm, "end": v(-59.93, 39.37) * mm});
            skArc(sketch, "E102", {"start": v(54.08, 48.07) * mm, "mid": v(0.07, 60) * mm, "end": v(-53.93, 48.07) * mm});
            skArc(sketch, "E103", {"start": v(60.02, 39.06) * mm, "mid": v(58.28, 44.38) * mm, "end": v(54.08, 48.07) * mm});
            skArc(sketch, "E104", {"start": v(-59.98, -39.31) * mm, "mid": v(-58.48, -44.08) * mm, "end": v(-54.9, -47.55) * mm});
            skArc(sketch, "E105", {"start": v(55.58, -47.23) * mm, "mid": v(58.75, -43.62) * mm, "end": v(60.05, -39) * mm});
            skArc(sketch, "E106", {"start": v(-54.9, -47.55) * mm, "mid": v(0.38, -60.03) * mm, "end": v(55.58, -47.23) * mm});
            skLineSegment(sketch, "E107", {"start": v(-59.93, 39.37) * mm, "end": v(-59.98, -39.31) * mm});
            skLineSegment(sketch, "E108", {"start": v(60.02, 39.06) * mm, "end": v(60.05, -39) * mm});
            skArc(sketch, "E109", {"start": v(-74.37, -64.15) * mm, "mid": v(-71.43, -71.37) * mm, "end": v(-64.28, -74.46) * mm});
            skLineSegment(sketch, "E110", {"start": v(-64.17, 74.37) * mm, "end": v(-32.82, 74.6) * mm});
            skLineSegment(sketch, "E111", {"start": v(33.17, 74.61) * mm, "end": v(64.62, 74.23) * mm});
            skLineSegment(sketch, "E112", {"start": v(-64.28, -74.46) * mm, "end": v(-32.98, -74.53) * mm});
            skLineSegment(sketch, "E113", {"start": v(33.01, -74.68) * mm, "end": v(64.6, -74.75) * mm});
            skArc(sketch, "E114", {"start": v(15.15, 104.58) * mm, "mid": v(0.18, 119.6) * mm, "end": v(-14.85, 104.64) * mm});
            skArc(sketch, "E115", {"start": v(-15.07, -104.6) * mm, "mid": v(-0.07, -119.6) * mm, "end": v(14.93, -104.6) * mm});
            skLineSegment(sketch, "E116", {"start": v(-32.82, 74.6) * mm, "end": v(33.17, 74.61) * mm});
            skLineSegment(sketch, "E117", {"start": v(-32.98, -74.53) * mm, "end": v(33.01, -74.68) * mm});
            skSolve(sketch);
        }
        {
            var Q0;
            Q0 = qSketchRegion(id + "F17", true);
            var Q1;
            Q1=makeQuery(id+"F2.opExtrude","CAP_FACE",FACE,{"disambiguationData":[OSD([sQuery(id+"F0.wireOp",EDGE,"E12"),sQuery(id+"F0.wireOp",EDGE,"E13"),sQuery(id+"F0.wireOp",EDGE,"E14"),sQuery(id+"F0.wireOp",EDGE,"E15"),sQuery(id+"F0.wireOp",EDGE,"E17.filletArc"),sQuery(id+"F0.wireOp",EDGE,"E18.filletArc"),sQuery(id+"F0.wireOp",EDGE,"E19.filletArc"),sQuery(id+"F0.wireOp",EDGE,"E20.filletArc"),sQuery(id+"F0.wireOp",EDGE,"E25.0"),sQuery(id+"F0.wireOp",EDGE,"E25.1"),sQuery(id+"F0.wireOp",EDGE,"E25.2"),sQuery(id+"F0.wireOp",EDGE,"E25.3"),sQuery(id+"F0.wireOp",EDGE,"E25.4"),sQuery(id+"F0.wireOp",EDGE,"E25.5"),sQuery(id+"F0.wireOp",EDGE,"E25.6"),sQuery(id+"F0.wireOp",EDGE,"E25.7")])],"isStart":false});
            extrude(context, id + "F18", {"entities" : qUnion([Q0]), "endBound" : BoundingType.UP_TO_SURFACE, "endBoundEntityFace" : qUnion([Q1]), "depth" : 25 * mm});
        }
        {
            var Q0;
            Q0=makeQuery(id+"F18.opExtrude","CAP_FACE",FACE,{"disambiguationData":[OSD([sQuery(id+"F17.wireOp",EDGE,"E79"),sQuery(id+"F17.wireOp",EDGE,"E80"),sQuery(id+"F17.wireOp",EDGE,"E81"),sQuery(id+"F17.wireOp",EDGE,"E82"),sQuery(id+"F17.wireOp",EDGE,"E83"),sQuery(id+"F17.wireOp",EDGE,"E90"),sQuery(id+"F17.wireOp",EDGE,"E91"),sQuery(id+"F17.wireOp",EDGE,"E92"),sQuery(id+"F17.wireOp",EDGE,"E93"),sQuery(id+"F17.wireOp",EDGE,"E101"),sQuery(id+"F17.wireOp",EDGE,"E102"),sQuery(id+"F17.wireOp",EDGE,"E103"),sQuery(id+"F17.wireOp",EDGE,"E104"),sQuery(id+"F17.wireOp",EDGE,"E105"),sQuery(id+"F17.wireOp",EDGE,"E106"),sQuery(id+"F17.wireOp",EDGE,"E107"),sQuery(id+"F17.wireOp",EDGE,"E108"),sQuery(id+"F17.wireOp",EDGE,"E109"),sQuery(id+"F17.wireOp",EDGE,"E110"),sQuery(id+"F17.wireOp",EDGE,"E111"),sQuery(id+"F17.wireOp",EDGE,"E112"),sQuery(id+"F17.wireOp",EDGE,"E113"),sQuery(id+"F17.wireOp",EDGE,"E116"),sQuery(id+"F17.wireOp",EDGE,"E117")])],"isStart":false});
            var sketch = newSketch(context, id + "F19", { "sketchPlane" : qUnion([Q0])});
            skCircle(sketch, "E118", {"center": v(0, -104.6) * mm, "radius": 6 * mm});
            skLineSegment(sketch, "E119", {"start": v(0, -74.6) * mm, "end": v(0, -104.6) * mm});
            skLineSegment(sketch, "E120", {"start": v(-32.89, -74.53) * mm, "end": v(-14.97, -92.53) * mm});
            skLineSegment(sketch, "E121", {"start": v(33.11, -74.68) * mm, "end": v(15.03, -92.68) * mm});
            skLineSegment(sketch, "E122", {"start": v(-14.97, -92.53) * mm, "end": v(-15, -104.6) * mm});
            skLineSegment(sketch, "E123", {"start": v(15.03, -92.68) * mm, "end": v(15, -104.6) * mm});
            skArc(sketch, "E124", {"start": v(-15, -104.6) * mm, "mid": v(0, -119.57) * mm, "end": v(15, -104.6) * mm});
            skLineSegment(sketch, "E125", {"start": v(0, -104.6) * mm, "end": v(0, 0) * mm});
            skLineSegment(sketch, "E126", {"start": v(0, 0) * mm, "end": v(74.33, 0) * mm});
            skLineSegment(sketch, "E127.MirrorCS", {"start": v(-14.97, 92.53) * mm, "end": v(-15, 104.6) * mm});
            skLineSegment(sketch, "E128.MirrorCS", {"start": v(-32.89, 74.53) * mm, "end": v(-14.97, 92.53) * mm});
            skLineSegment(sketch, "E129", {"start": v(-32.82, 74.6) * mm, "end": v(33.17, 74.61) * mm});
            skLineSegment(sketch, "E130", {"start": v(-32.89, -74.53) * mm, "end": v(33.11, -74.68) * mm});
            skLineSegment(sketch, "E131", {"start": v(-32.82, 74.6) * mm, "end": v(-14.97, 92.53) * mm});
            skLineSegment(sketch, "E132", {"start": v(33.17, 74.61) * mm, "end": v(-32.82, 74.6) * mm});
            skArc(sketch, "E133", {"start": v(15, 104.6) * mm, "mid": v(0, 119.57) * mm, "end": v(-15, 104.6) * mm});
            skLineSegment(sketch, "E134", {"start": v(15, 104.6) * mm, "end": v(15.03, 92.68) * mm});
            skLineSegment(sketch, "E135", {"start": v(15.03, 92.68) * mm, "end": v(33.17, 74.61) * mm});
            skCircle(sketch, "E136", {"center": v(0, 104.57) * mm, "radius": 6 * mm});
            skSolve(sketch);
        }
        {
            var Q0;
            Q0=makeQuery(id+"F19.imprint","IMPRINT",FACE,{"disambiguationData":[TD([[makeQuery(id+"F19.imprint","IMPRINT",EDGE,{"derivedFrom":sQuery(id+"F19.wireOp",EDGE,"E118")}),-1.0]])]});
            var Q1;
            Q1=makeQuery(id+"F18.opExtrude","CAP_FACE",FACE,{"disambiguationData":[OSD([sQuery(id+"F17.wireOp",EDGE,"E79"),sQuery(id+"F17.wireOp",EDGE,"E80"),sQuery(id+"F17.wireOp",EDGE,"E81"),sQuery(id+"F17.wireOp",EDGE,"E82"),sQuery(id+"F17.wireOp",EDGE,"E83"),sQuery(id+"F17.wireOp",EDGE,"E90"),sQuery(id+"F17.wireOp",EDGE,"E91"),sQuery(id+"F17.wireOp",EDGE,"E92"),sQuery(id+"F17.wireOp",EDGE,"E93"),sQuery(id+"F17.wireOp",EDGE,"E101"),sQuery(id+"F17.wireOp",EDGE,"E102"),sQuery(id+"F17.wireOp",EDGE,"E103"),sQuery(id+"F17.wireOp",EDGE,"E104"),sQuery(id+"F17.wireOp",EDGE,"E105"),sQuery(id+"F17.wireOp",EDGE,"E106"),sQuery(id+"F17.wireOp",EDGE,"E107"),sQuery(id+"F17.wireOp",EDGE,"E108"),sQuery(id+"F17.wireOp",EDGE,"E109"),sQuery(id+"F17.wireOp",EDGE,"E110"),sQuery(id+"F17.wireOp",EDGE,"E111"),sQuery(id+"F17.wireOp",EDGE,"E112"),sQuery(id+"F17.wireOp",EDGE,"E113"),sQuery(id+"F17.wireOp",EDGE,"E116"),sQuery(id+"F17.wireOp",EDGE,"E117")])],"isStart":true});
            extrude(context, id + "F20", {"entities" : qUnion([Q0]), "operationType" : NewBodyOperationType.ADD, "endBound" : BoundingType.UP_TO_SURFACE, "oppositeDirection" : true, "endBoundEntityFace" : qUnion([Q1]), "depth" : 25 * mm});
        }
        {
            var Q0;
            Q0 = qSketchRegion(id + "F19", true);
            var Q1;
            Q1=makeQuery(id+"F20.boolean.opBoolean","MERGE",FACE,{"derivedFrom":[makeQuery(id+"F18.opExtrude","CAP_FACE",FACE,{"disambiguationData":[OSD([sQuery(id+"F17.wireOp",EDGE,"E79"),sQuery(id+"F17.wireOp",EDGE,"E80"),sQuery(id+"F17.wireOp",EDGE,"E81"),sQuery(id+"F17.wireOp",EDGE,"E82"),sQuery(id+"F17.wireOp",EDGE,"E83"),sQuery(id+"F17.wireOp",EDGE,"E90"),sQuery(id+"F17.wireOp",EDGE,"E91"),sQuery(id+"F17.wireOp",EDGE,"E92"),sQuery(id+"F17.wireOp",EDGE,"E93"),sQuery(id+"F17.wireOp",EDGE,"E101"),sQuery(id+"F17.wireOp",EDGE,"E102"),sQuery(id+"F17.wireOp",EDGE,"E103"),sQuery(id+"F17.wireOp",EDGE,"E104"),sQuery(id+"F17.wireOp",EDGE,"E105"),sQuery(id+"F17.wireOp",EDGE,"E106"),sQuery(id+"F17.wireOp",EDGE,"E107"),sQuery(id+"F17.wireOp",EDGE,"E108"),sQuery(id+"F17.wireOp",EDGE,"E109"),sQuery(id+"F17.wireOp",EDGE,"E110"),sQuery(id+"F17.wireOp",EDGE,"E111"),sQuery(id+"F17.wireOp",EDGE,"E112"),sQuery(id+"F17.wireOp",EDGE,"E113"),sQuery(id+"F17.wireOp",EDGE,"E116"),sQuery(id+"F17.wireOp",EDGE,"E117")])],"isStart":true}),makeQuery(id+"F20.opExtrude","CAP_FACE",FACE,{"disambiguationData":[OSD([sQuery(id+"F19.wireOp",EDGE,"E118"),sQuery(id+"F19.wireOp",EDGE,"E120"),sQuery(id+"F19.wireOp",EDGE,"E121"),sQuery(id+"F19.wireOp",EDGE,"E122"),sQuery(id+"F19.wireOp",EDGE,"E123"),sQuery(id+"F19.wireOp",EDGE,"E124"),sQuery(id+"F19.wireOp",EDGE,"E130")])],"isStart":false})]});
            extrude(context, id + "F21", {"entities" : qUnion([Q0]), "operationType" : NewBodyOperationType.ADD, "endBound" : BoundingType.UP_TO_SURFACE, "oppositeDirection" : true, "endBoundEntityFace" : qUnion([Q1]), "depth" : 25 * mm});
        }
    });
